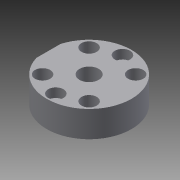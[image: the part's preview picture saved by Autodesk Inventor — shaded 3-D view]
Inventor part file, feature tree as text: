
AUTODESK INVENTOR PART (.ipt)
format: ipt  version: 2014 SP2 (Build 180246200, 246)  size: 264,192 bytes
history: native  units: in
note: dims shown in document units (in); Inventor stores cm internally (conversion verified against a paired STEP export)
features: other x308, sketch x8, hole x4, revolve x3, extrude x1, thread x1, pattern_linear x1
ambient origin geometry x8: Origin, YZ Plane, XZ Plane, XY Plane, X Axis, Y Axis, Z Axis, Center Point
bodies: Solid1 (feature_tree)
feature tree (326):
  revolve  "Revolution1"  [1 undecoded]
  extrude  "Extrusion1"  Depth=0.1831in TaperAngle=0.0deg
  revolve  "Revolution2"  Angle=360.0deg
  thread  "Thread1"  [1 undecoded]
  hole  "Hole1"  [1 undecoded]
  revolve  "Revolution3"  [1 undecoded]
  hole  "Hole2"  [1 undecoded]
  hole  "Hole3"  [1 undecoded]
  hole  "Hole4"  [1 undecoded]
  pattern_linear  "Rectangular Pattern1"  [2 undecoded]
  other  "a1_XY"
  other  "a1_YZ"
  other  "a1_ZX"
  other  "a1_X"
  other  "a1_Y"
  other  "a1_Z"
  other  "a1_Center"
  other  "a2_XY"
  other  "a2_YZ"
  other  "a2_ZX"
  other  "a2_X"
  other  "a2_Y"
  other  "a2_Z"
  other  "a2_Center"
  other  "ab_tr1_XY"
  other  "ab_tr1_YZ"
  other  "ab_tr1_ZX"
  other  "ab_tr1_X"
  other  "ab_tr1_Y"
  other  "ab_tr1_Z"
  other  "ab_tr1_Center"
  other  "ab_tr2_XY"
  other  "ab_tr2_YZ"
  other  "ab_tr2_ZX"
  other  "ab_tr2_X"
  other  "ab_tr2_Y"
  other  "ab_tr2_Z"
  other  "ab_tr2_Center"
  other  "ab_tr3_XY"
  other  "ab_tr3_YZ"
  other  "ab_tr3_ZX"
  other  "ab_tr3_X"
  other  "ab_tr3_Y"
  other  "ab_tr3_Z"
  other  "ab_tr3_Center"
  other  "ab_tr4_XY"
  other  "ab_tr4_YZ"
  other  "ab_tr4_ZX"
  other  "ab_tr4_X"
  other  "ab_tr4_Y"
  other  "ab_tr4_Z"
  other  "ab_tr4_Center"
  other  "ar3_XY"
  other  "ar3_YZ"
  other  "ar3_ZX"
  other  "ar3_X"
  other  "ar3_Y"
  other  "ar3_Z"
  other  "ar3_Center"
  other  "ar4_XY"
  other  "ar4_YZ"
  other  "ar4_ZX"
  other  "ar4_X"
  other  "ar4_Y"
  other  "ar4_Z"
  other  "ar4_Center"
  other  "ar5_XY"
  other  "ar5_YZ"
  other  "ar5_ZX"
  other  "ar5_X"
  other  "ar5_Y"
  other  "ar5_Z"
  other  "ar5_Center"
  other  "ar6_XY"
  other  "ar6_YZ"
  other  "ar6_ZX"
  other  "ar6_X"
  other  "ar6_Y"
  other  "ar6_Z"
  other  "ar6_Center"
  other  "b1_XY"
  other  "b1_YZ"
  other  "b1_ZX"
  other  "b1_X"
  other  "b1_Y"
  other  "b1_Z"
  other  "b1_Center"
  other  "j_XY"
  other  "j_YZ"
  other  "j_ZX"
  other  "j_X"
  other  "j_Y"
  other  "j_Z"
  other  "j_Center"
  other  "k1_XY"
  other  "k1_YZ"
  other  "k1_ZX"
  other  "k1_X"
  other  "k1_Y"
  other  "k1_Z"
  other  "k1_Center"
  other  "k2_XY"
  other  "k2_YZ"
  other  "k2_ZX"
  other  "k2_X"
  other  "k2_Y"
  other  "k2_Z"
  other  "k2_Center"
  other  "l1_XY"
  other  "l1_YZ"
  other  "l1_ZX"
  other  "l1_X"
  other  "l1_Y"
  other  "l1_Z"
  other  "l1_Center"
  other  "l2_XY"
  other  "l2_YZ"
  other  "l2_ZX"
  other  "l2_X"
  other  "l2_Y"
  other  "l2_Z"
  other  "l2_Center"
  other  "nut_XY"
  other  "nut_YZ"
  other  "nut_ZX"
  other  "nut_X"
  other  "nut_Y"
  other  "nut_Z"
  other  "nut_Center"
  other  "po1_XY"
  other  "po1_YZ"
  other  "po1_ZX"
  other  "po1_X"
  other  "po1_Y"
  other  "po1_Z"
  other  "po1_Center"
  other  "po2_XY"
  other  "po2_YZ"
  other  "po2_ZX"
  other  "po2_X"
  other  "po2_Y"
  other  "po2_Z"
  other  "po2_Center"
  other  "po3_XY"
  other  "po3_YZ"
  other  "po3_ZX"
  other  "po3_X"
  other  "po3_Y"
  other  "po3_Z"
  other  "po3_Center"
  other  "po4_XY"
  other  "po4_YZ"
  other  "po4_ZX"
  other  "po4_X"
  other  "po4_Y"
  other  "po4_Z"
  other  "po4_Center"
  other  "r7_XY"
  other  "r7_YZ"
  other  "r7_ZX"
  other  "r7_X"
  other  "r7_Y"
  other  "r7_Z"
  other  "r7_Center"
  other  "r71_XY"
  other  "r71_YZ"
  other  "r71_ZX"
  other  "r71_X"
  other  "r71_Y"
  other  "r71_Z"
  other  "r71_Center"
  other  "r72_XY"
  other  "r72_YZ"
  other  "r72_ZX"
  other  "r72_X"
  other  "r72_Y"
  other  "r72_Z"
  other  "r72_Center"
  other  "r73_XY"
  other  "r73_YZ"
  other  "r73_ZX"
  other  "r73_X"
  other  "r73_Y"
  other  "r73_Z"
  other  "r73_Center"
  other  "rg_XY"
  other  "rg_YZ"
  other  "rg_ZX"
  other  "rg_X"
  other  "rg_Y"
  other  "rg_Z"
  other  "rg_Center"
  other  "rh_XY"
  other  "rh_YZ"
  other  "rh_ZX"
  other  "rh_X"
  other  "rh_Y"
  other  "rh_Z"
  other  "rh_Center"
  other  "rs_1_XY"
  other  "rs_1_YZ"
  other  "rs_1_ZX"
  other  "rs_1_X"
  other  "rs_1_Y"
  other  "rs_1_Z"
  other  "rs_1_Center"
  other  "rs_2_XY"
  other  "rs_2_YZ"
  other  "rs_2_ZX"
  other  "rs_2_X"
  other  "rs_2_Y"
  other  "rs_2_Z"
  other  "rs_2_Center"
  other  "rs_3_XY"
  other  "rs_3_YZ"
  other  "rs_3_ZX"
  other  "rs_3_X"
  other  "rs_3_Y"
  other  "rs_3_Z"
  other  "rs_3_Center"
  other  "rs_4_XY"
  other  "rs_4_YZ"
  other  "rs_4_ZX"
  other  "rs_4_X"
  other  "rs_4_Y"
  other  "rs_4_Z"
  other  "rs_4_Center"
  other  "sc1_XY"
  other  "sc1_YZ"
  other  "sc1_ZX"
  other  "sc1_X"
  other  "sc1_Y"
  other  "sc1_Z"
  other  "sc1_Center"
  other  "sc2_XY"
  other  "sc2_YZ"
  other  "sc2_ZX"
  other  "sc2_X"
  other  "sc2_Y"
  other  "sc2_Z"
  other  "sc2_Center"
  other  "sc3_XY"
  other  "sc3_YZ"
  other  "sc3_ZX"
  other  "sc3_X"
  other  "sc3_Y"
  other  "sc3_Z"
  other  "sc3_Center"
  other  "sc4_XY"
  other  "sc4_YZ"
  other  "sc4_ZX"
  other  "sc4_X"
  other  "sc4_Y"
  other  "sc4_Z"
  other  "sc4_Center"
  other  "to_dummy_XY"
  other  "to_dummy_YZ"
  other  "to_dummy_ZX"
  other  "to_dummy_X"
  other  "to_dummy_Y"
  other  "to_dummy_Z"
  other  "to_dummy_Center"
  other  "to_nut_XY"
  other  "to_nut_YZ"
  other  "to_nut_ZX"
  other  "to_nut_X"
  other  "to_nut_Y"
  other  "to_nut_Z"
  other  "to_nut_Center"
  other  "to_rod_XY"
  other  "to_rod_YZ"
  other  "to_rod_ZX"
  other  "to_rod_X"
  other  "to_rod_Y"
  other  "to_rod_Z"
  other  "to_rod_Center"
  other  "to_tube_XY"
  other  "to_tube_YZ"
  other  "to_tube_ZX"
  other  "to_tube_X"
  other  "to_tube_Y"
  other  "to_tube_Z"
  other  "to_tube_Center"
  other  "to_wiper_XY"
  other  "to_wiper_YZ"
  other  "to_wiper_ZX"
  other  "to_wiper_X"
  other  "to_wiper_Y"
  other  "to_wiper_Z"
  other  "to_wiper_Center"
  other  "track1_XY"
  other  "track1_YZ"
  other  "track1_ZX"
  other  "track1_X"
  other  "track1_Y"
  other  "track1_Z"
  other  "track1_Center"
  other  "track2_XY"
  other  "track2_YZ"
  other  "track2_ZX"
  other  "track2_X"
  other  "track2_Y"
  other  "track2_Z"
  other  "track2_Center"
  other  "track3_XY"
  other  "track3_YZ"
  other  "track3_ZX"
  other  "track3_X"
  other  "track3_Y"
  other  "track3_Z"
  other  "track3_Center"
  other  "track4_XY"
  other  "track4_YZ"
  other  "track4_ZX"
  other  "track4_X"
  other  "track4_Y"
  other  "track4_Z"
  other  "track4_Center"
  sketch  "Sketch_1"  dims[d0=360.0deg d1=0.344in d2=0.0in]
  sketch  "Sketch_63"
  sketch  "Sketch_37"  dims[d41=0.0in d42=0.0in d43=0.0in d44=0.0in d45=0.0in d46=0.0in d47=0.0in d48=0.0in d49=0.0in d50=0.0in d51=0.0in d52=0.0in d53=0.0in d54=0.0in d55=0.0in d56=0.0in d57=0.0in d58=0.0in d59=0.0in d60=0.0in d61=0.0in d62=0.0in d63=0.0in d64=0.0in d65=0.0in d66=0.0in d67=0.0in d68=0.0in d69=0.0in d70=0.0in]
  sketch  "Sketch4"  dims[d3=360.0deg d4=0.1831in d5=0.0in]
  sketch  "Sketch_9"  dims[d28=0.1285in d29=0.75in d30=0.2in d31=0.15in d32=0.5635in d33=0.344in d34=0.0in d35=0.7874in d37=0.6109in d38=0.7874in d40=0.6109in]
  sketch  "Sketch6"  dims[d6=0.252in d7=0.75in d8=0.375in d9=0.25in d10=0.5635in d11=0.344in d12=0.0in d13=360.0deg]
  sketch  "Sketch7"  dims[d14=0.1285in d15=0.75in d16=0.2in d17=0.12in d18=0.5635in d19=0.344in d20=0.0in]
  sketch  "Sketch8"  dims[d21=0.1285in d22=0.75in d23=0.2in d24=0.12in d25=0.5635in d26=0.344in d27=0.0in]
note: 9 required parameter values undecoded (feature->parameter linkage not recoverable at this tier; creation-order binding heuristic only, values carry confidence <= 0.55)